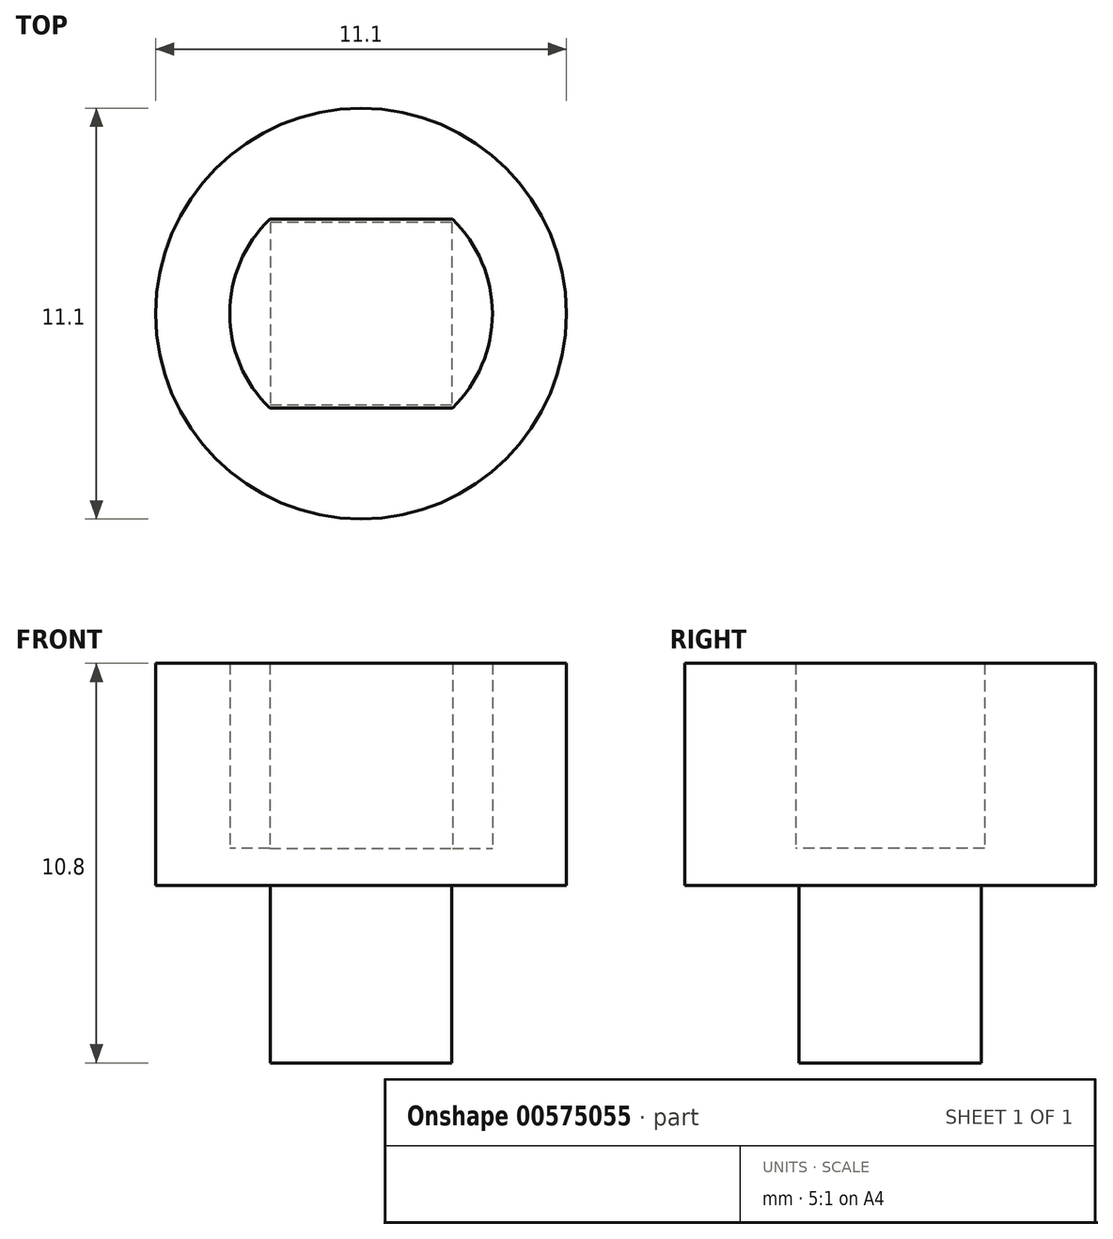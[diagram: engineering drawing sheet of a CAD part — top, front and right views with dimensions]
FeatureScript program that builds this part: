
annotation { "Feature Type Name" : "Feature", "Feature Type Description" : "" }
export const myFeature = defineFeature(function(context is Context, id is Id, definition is map)
    precondition{}
    {
        {
            var Q0;
            Q0=qCreatedBy(makeId("Top.planeOp"),FACE);
            var sketch = newSketch(context, id + "F0", { "sketchPlane" : qUnion([Q0])});
            skLineSegment(sketch, "E0.bottom", {"start": v(-2.47, 2.55) * mm, "end": v(2.47, 2.55) * mm});
            skLineSegment(sketch, "E0.top", {"start": v(-2.47, -2.55) * mm, "end": v(2.47, -2.55) * mm});
            skLineSegment(sketch, "E0.left", {"start": v(-2.47, 2.55) * mm, "end": v(-2.47, -2.55) * mm});
            skLineSegment(sketch, "E0.right", {"start": v(2.47, 2.55) * mm, "end": v(2.47, -2.55) * mm});
            skArc(sketch, "E1", {"start": v(-2.47, 2.55) * mm, "mid": v(-3.55, 0) * mm, "end": v(-2.47, -2.55) * mm});
            skArc(sketch, "E2.MirrorCS", {"start": v(2.47, 2.55) * mm, "mid": v(3.55, 0) * mm, "end": v(2.47, -2.55) * mm});
            skCircle(sketch, "E3", {"center": v(0, 0) * mm, "radius": 5.55 * mm});
            skSolve(sketch);
        }
        {
            var Q0;
            Q0=makeQuery(id+"F0.imprint","IMPRINT",FACE,{"disambiguationData":[TD([[makeQuery(id+"F0.imprint","IMPRINT",EDGE,{"derivedFrom":sQuery(id+"F0.wireOp",EDGE,"E0.bottom")}),1.0]])]});
            extrude(context, id + "F1", {"entities" : qUnion([Q0]), "depth" : 5 * mm, "offsetDistance" : 25 * mm});
        }
        {
            var Q0;
            Q0=makeQuery(id+"F0.imprint","IMPRINT",FACE,{"disambiguationData":[TD([[makeQuery(id+"F0.imprint","IMPRINT",EDGE,{"derivedFrom":sQuery(id+"F0.wireOp",EDGE,"E0.bottom")}),1.0]])]});
            var Q1;
            Q1=makeQuery(id+"F0.imprint","IMPRINT",FACE,{"disambiguationData":[TD([[makeQuery(id+"F0.imprint","IMPRINT",EDGE,{"derivedFrom":sQuery(id+"F0.wireOp",EDGE,"E0.right")}),1.0]])]});
            var Q2;
            Q2=makeQuery(id+"F0.imprint","IMPRINT",FACE,{"disambiguationData":[TD([[makeQuery(id+"F0.imprint","IMPRINT",EDGE,{"derivedFrom":sQuery(id+"F0.wireOp",EDGE,"E0.bottom")}),-1.0]])]});
            var Q3;
            Q3=makeQuery(id+"F0.imprint","IMPRINT",FACE,{"disambiguationData":[TD([[makeQuery(id+"F0.imprint","IMPRINT",EDGE,{"derivedFrom":sQuery(id+"F0.wireOp",EDGE,"E0.left")}),-1.0]])]});
            extrude(context, id + "F2", {"entities" : qUnion([Q0, Q1, Q2, Q3]), "operationType" : NewBodyOperationType.ADD, "oppositeDirection" : true, "depth" : 1 * mm, "offsetDistance" : 25 * mm});
        }
        {
            var Q0;
            Q0=makeQuery(id+"F2.opExtrude","CAP_FACE",FACE,{"disambiguationData":[OSD([sQuery(id+"F0.wireOp",EDGE,"E3")])],"isStart":false});
            var sketch = newSketch(context, id + "F3", { "sketchPlane" : qUnion([Q0])});
            skLineSegment(sketch, "E4.bottom", {"start": v(2.45, -2.47) * mm, "end": v(-2.45, -2.47) * mm});
            skLineSegment(sketch, "E4.top", {"start": v(2.45, 2.47) * mm, "end": v(-2.45, 2.47) * mm});
            skLineSegment(sketch, "E4.left", {"start": v(2.45, -2.47) * mm, "end": v(2.45, 2.47) * mm});
            skLineSegment(sketch, "E4.right", {"start": v(-2.45, -2.47) * mm, "end": v(-2.45, 2.47) * mm});
            skPoint(sketch, "E4.middle", {"position": v(0, 0) * mm});
            skSolve(sketch);
        }
        {
            var Q0;
            Q0 = qSketchRegion(id + "F3", true);
            extrude(context, id + "F4", {"entities" : qUnion([Q0]), "operationType" : NewBodyOperationType.ADD, "depth" : 4.8 * mm, "offsetDistance" : 25 * mm});
        }
    });
